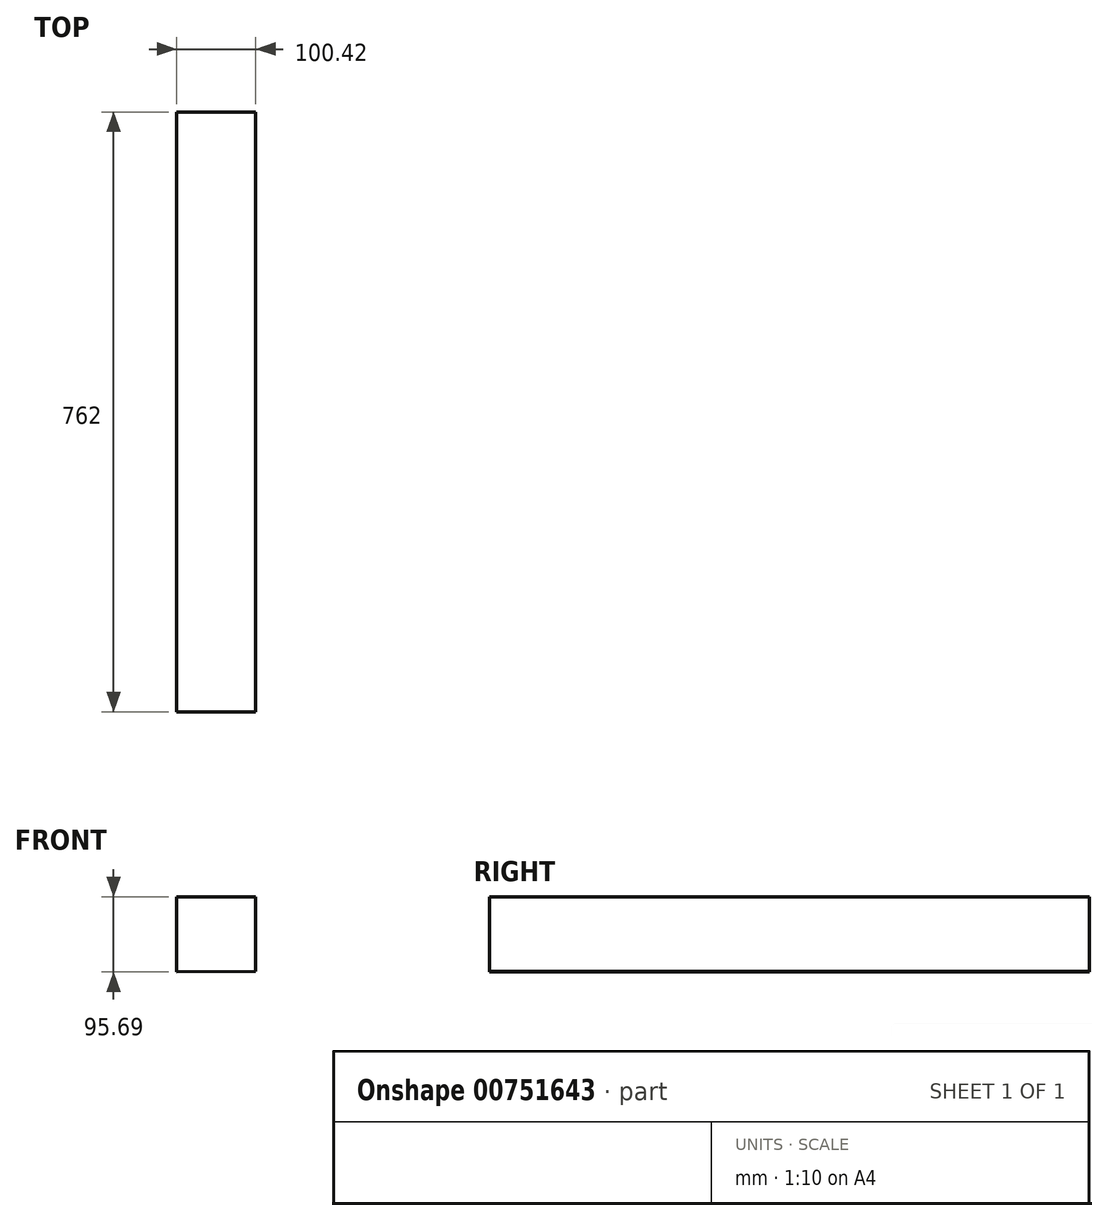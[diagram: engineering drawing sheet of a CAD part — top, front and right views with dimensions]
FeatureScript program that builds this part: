
annotation { "Feature Type Name" : "Feature", "Feature Type Description" : "" }
export const myFeature = defineFeature(function(context is Context, id is Id, definition is map)
    precondition{}
    {
        {
            var Q0;
            Q0=qCreatedBy(makeId("Front.planeOp"),FACE);
            var sketch = newSketch(context, id + "F0", { "sketchPlane" : qUnion([Q0])});
            skLineSegment(sketch, "E0", {"start": v(39.27, -41.96) * mm, "end": v(39.27, 53.05) * mm});
            skLineSegment(sketch, "E1", {"start": v(39.27, 53.05) * mm, "end": v(-61.15, 53.05) * mm});
            skLineSegment(sketch, "E2", {"start": v(-61.15, 53.05) * mm, "end": v(-61.15, -42.64) * mm});
            skLineSegment(sketch, "E3", {"start": v(-61.15, -42.64) * mm, "end": v(39.27, -41.96) * mm});
            skLineSegment(sketch, "E4", {"start": v(-30.13, 53.05) * mm, "end": v(-44.85, 130.75) * mm, "construction": true});
            skLineSegment(sketch, "E5", {"start": v(-44.85, 130.75) * mm, "end": v(-88.18, 122.54) * mm, "construction": true});
            skLineSegment(sketch, "E6", {"start": v(-88.18, 122.54) * mm, "end": v(-104.66, 50.86) * mm, "construction": true});
            skLineSegment(sketch, "E7", {"start": v(-104.66, 50.86) * mm, "end": v(-97.3, -10.95) * mm, "construction": true});
            skLineSegment(sketch, "E8", {"start": v(-97.3, -10.95) * mm, "end": v(56.9, 23.2) * mm, "construction": true});
            skLineSegment(sketch, "E9", {"start": v(56.9, 23.2) * mm, "end": v(12.27, 96.39) * mm, "construction": true});
            skLineSegment(sketch, "E10", {"start": v(12.27, 96.39) * mm, "end": v(-55.79, 125.4) * mm, "construction": true});
            skSolve(sketch);
        }
        {
            var Q0;
            Q0=makeQuery(id+"F0.imprint","IMPRINT",FACE,{"disambiguationData":[TD([[makeQuery(id+"F0.imprint","IMPRINT",EDGE,{"derivedFrom":sQuery(id+"F0.wireOp",EDGE,"E0")}),1.0]])]});
            extrude(context, id + "F1", {"entities" : qUnion([Q0]), "depth" : 762 * mm, "offsetDistance" : 25.4 * mm});
        }
    });
